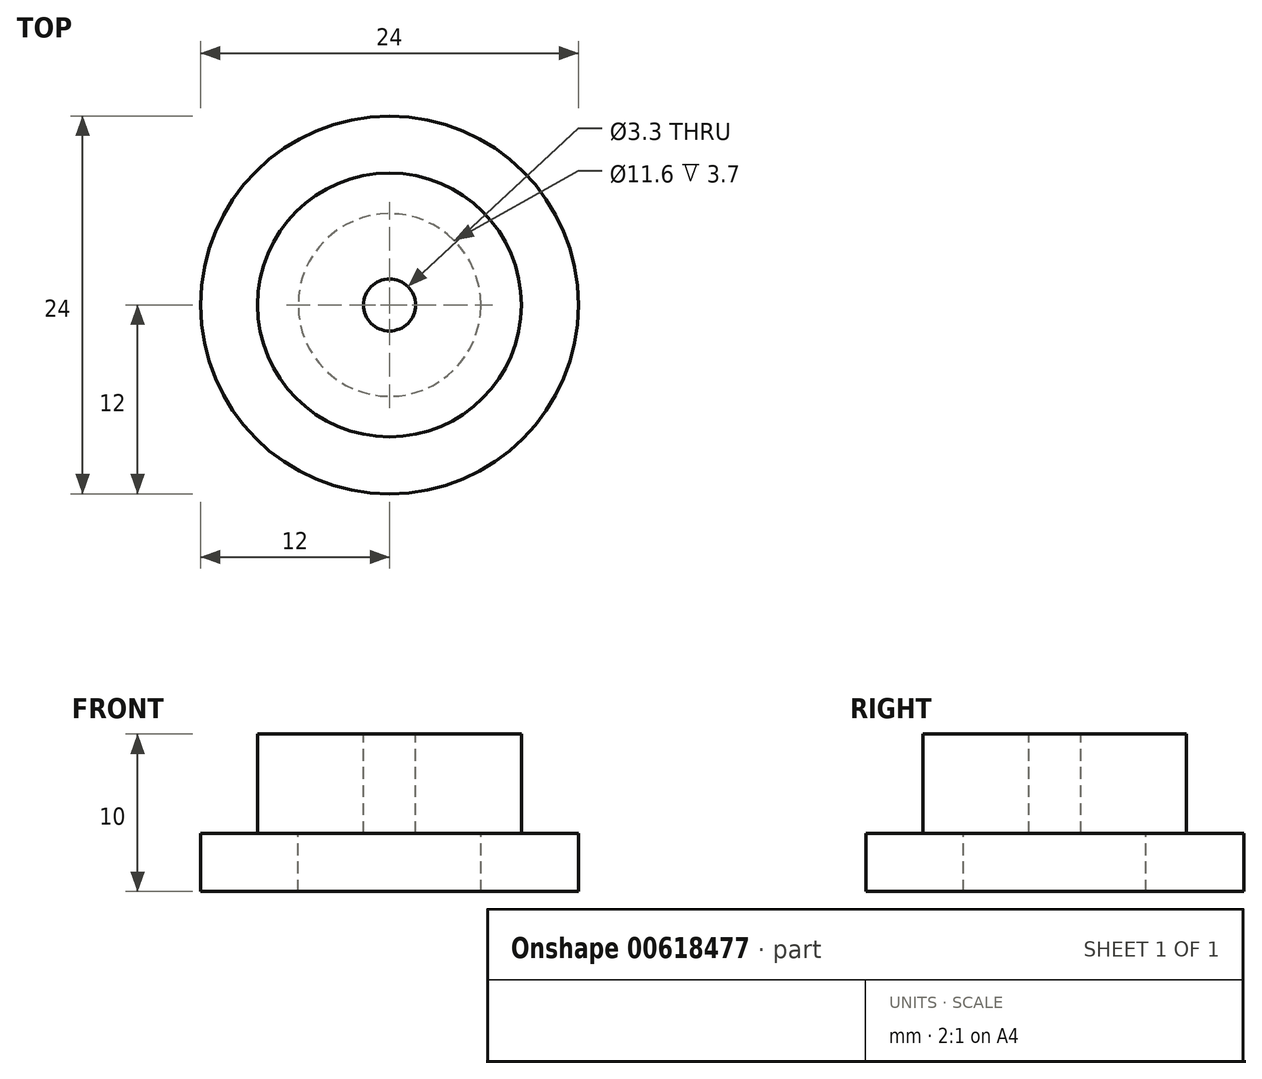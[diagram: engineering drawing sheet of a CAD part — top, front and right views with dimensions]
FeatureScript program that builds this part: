
annotation { "Feature Type Name" : "Feature", "Feature Type Description" : "" }
export const myFeature = defineFeature(function(context is Context, id is Id, definition is map)
    precondition{}
    {
        {
            var Q0;
            Q0=qCreatedBy(makeId("Front.planeOp"),FACE);
            var sketch = newSketch(context, id + "F0", { "sketchPlane" : qUnion([Q0])});
            skLineSegment(sketch, "E0", {"start": v(1.65, 10) * mm, "end": v(1.65, 3.7) * mm});
            skLineSegment(sketch, "E1", {"start": v(1.65, 3.7) * mm, "end": v(5.8, 3.7) * mm});
            skLineSegment(sketch, "E2", {"start": v(5.8, 3.7) * mm, "end": v(5.8, 0) * mm});
            skLineSegment(sketch, "E3", {"start": v(5.8, 0) * mm, "end": v(12, 0) * mm});
            skLineSegment(sketch, "E4", {"start": v(12, 0) * mm, "end": v(12, 3.7) * mm});
            skLineSegment(sketch, "E5", {"start": v(12, 3.7) * mm, "end": v(8.38, 3.7) * mm});
            skLineSegment(sketch, "E6", {"start": v(8.38, 3.7) * mm, "end": v(8.38, 10) * mm});
            skLineSegment(sketch, "E7", {"start": v(1.65, 10) * mm, "end": v(8.38, 10) * mm});
            skLineSegment(sketch, "E8", {"start": v(0, 35.93) * mm, "end": v(0, -23.08) * mm, "construction": true});
            skSolve(sketch);
        }
        {
            var Q0;
            Q0 = qSketchRegion(id + "F0", true);
            var Q1;
            Q1=sQuery(id+"F0.wireOp",EDGE,"E8");
            revolve(context, id + "F1", {"entities" : qUnion([Q0]), "axis" : qUnion([Q1]), "revolveType" : RevolveType.FULL});
        }
    });
